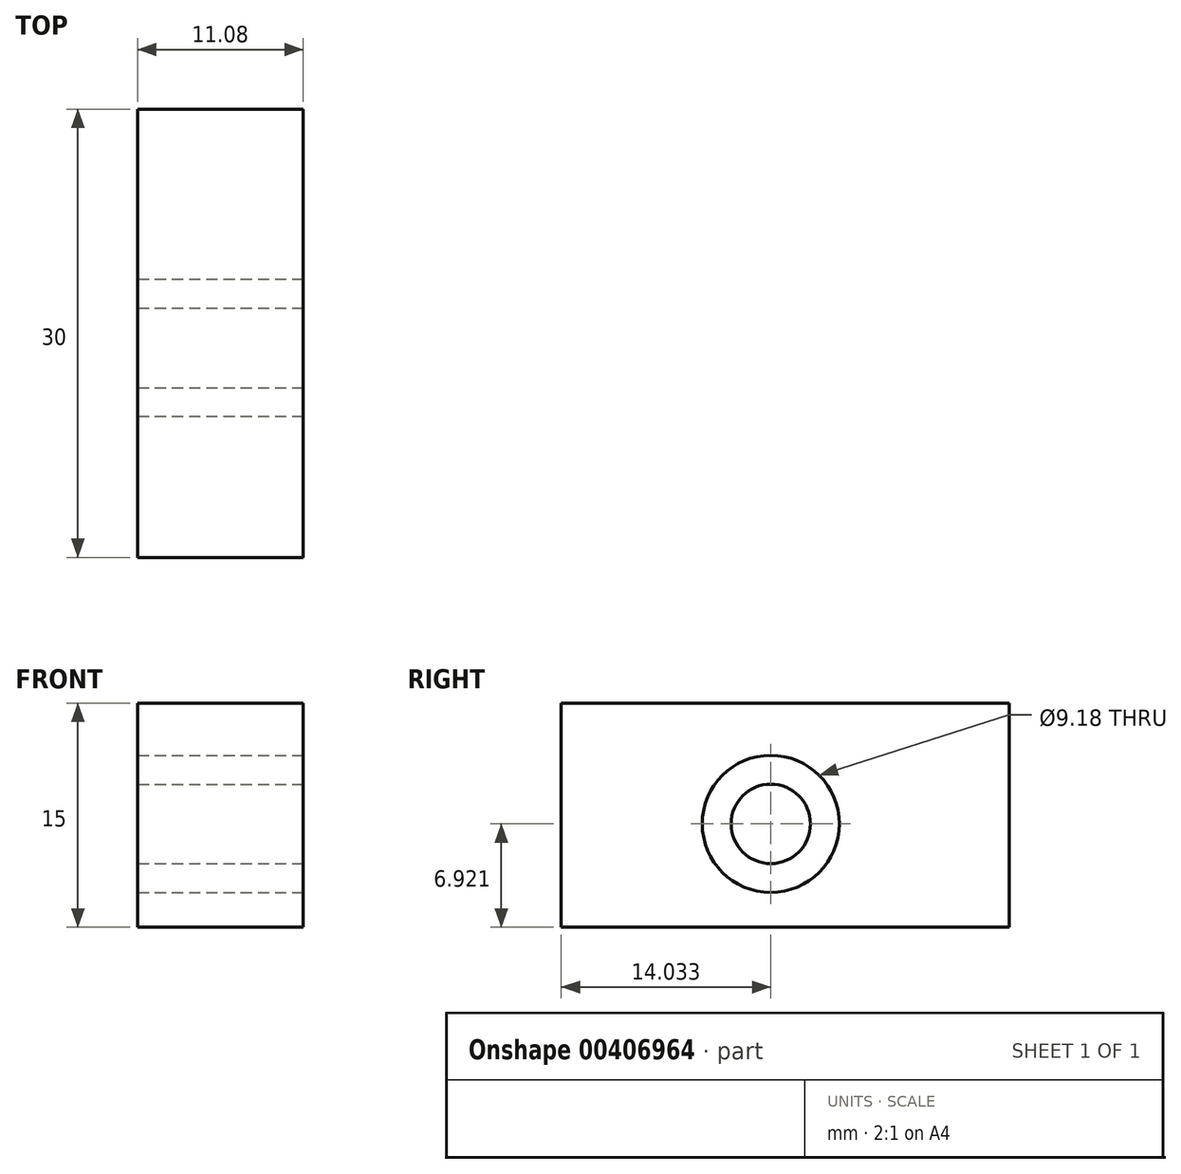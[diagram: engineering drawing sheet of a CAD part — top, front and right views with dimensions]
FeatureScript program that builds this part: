
annotation { "Feature Type Name" : "Feature", "Feature Type Description" : "" }
export const myFeature = defineFeature(function(context is Context, id is Id, definition is map)
    precondition{}
    {
        {
            var Q0;
            Q0=qCreatedBy(makeId("Front.planeOp"),FACE);
            var sketch = newSketch(context, id + "F0", { "sketchPlane" : qUnion([Q0])});
            skLineSegment(sketch, "E0.bottom", {"start": v(5.54, -3.2) * mm, "end": v(-5.54, -3.2) * mm});
            skLineSegment(sketch, "E0.top", {"start": v(5.54, 11.8) * mm, "end": v(-5.54, 11.8) * mm});
            skLineSegment(sketch, "E0.left", {"start": v(5.54, -3.2) * mm, "end": v(5.54, 11.8) * mm});
            skLineSegment(sketch, "E0.right", {"start": v(-5.54, -3.2) * mm, "end": v(-5.54, 11.8) * mm});
            skPoint(sketch, "E0.middle", {"position": v(0, 4.3) * mm});
            skSolve(sketch);
        }
        {
            var Q0;
            Q0=makeQuery(id+"F0.imprint","IMPRINT",FACE,{"disambiguationData":[TD([[makeQuery(id+"F0.imprint","IMPRINT",EDGE,{"derivedFrom":sQuery(id+"F0.wireOp",EDGE,"E0.bottom")}),-1.0]])]});
            extrude(context, id + "F1", {"entities" : qUnion([Q0]), "depth" : 30 * mm});
        }
        {
            var Q0;
            Q0=makeQuery(id+"F1.opExtrude","SWEPT_FACE",FACE,{"disambiguationData":[OSD([sQuery(id+"F0.wireOp",EDGE,"E0.left")])]});
            var sketch = newSketch(context, id + "F2", { "sketchPlane" : qUnion([Q0])});
            skCircle(sketch, "E1", {"center": v(-15.97, 3.71) * mm, "radius": 4.59 * mm});
            skCircle(sketch, "E2", {"center": v(-15.97, 3.71) * mm, "radius": 2.66 * mm});
            skSolve(sketch);
        }
        {
            var Q0;
            Q0 = qSketchRegion(id + "F2", true);
            extrude(context, id + "F3", {"entities" : qUnion([Q0]), "operationType" : NewBodyOperationType.REMOVE, "endBound" : BoundingType.THROUGH_ALL, "oppositeDirection" : true, "depth" : 25.4 * mm});
        }
    });
